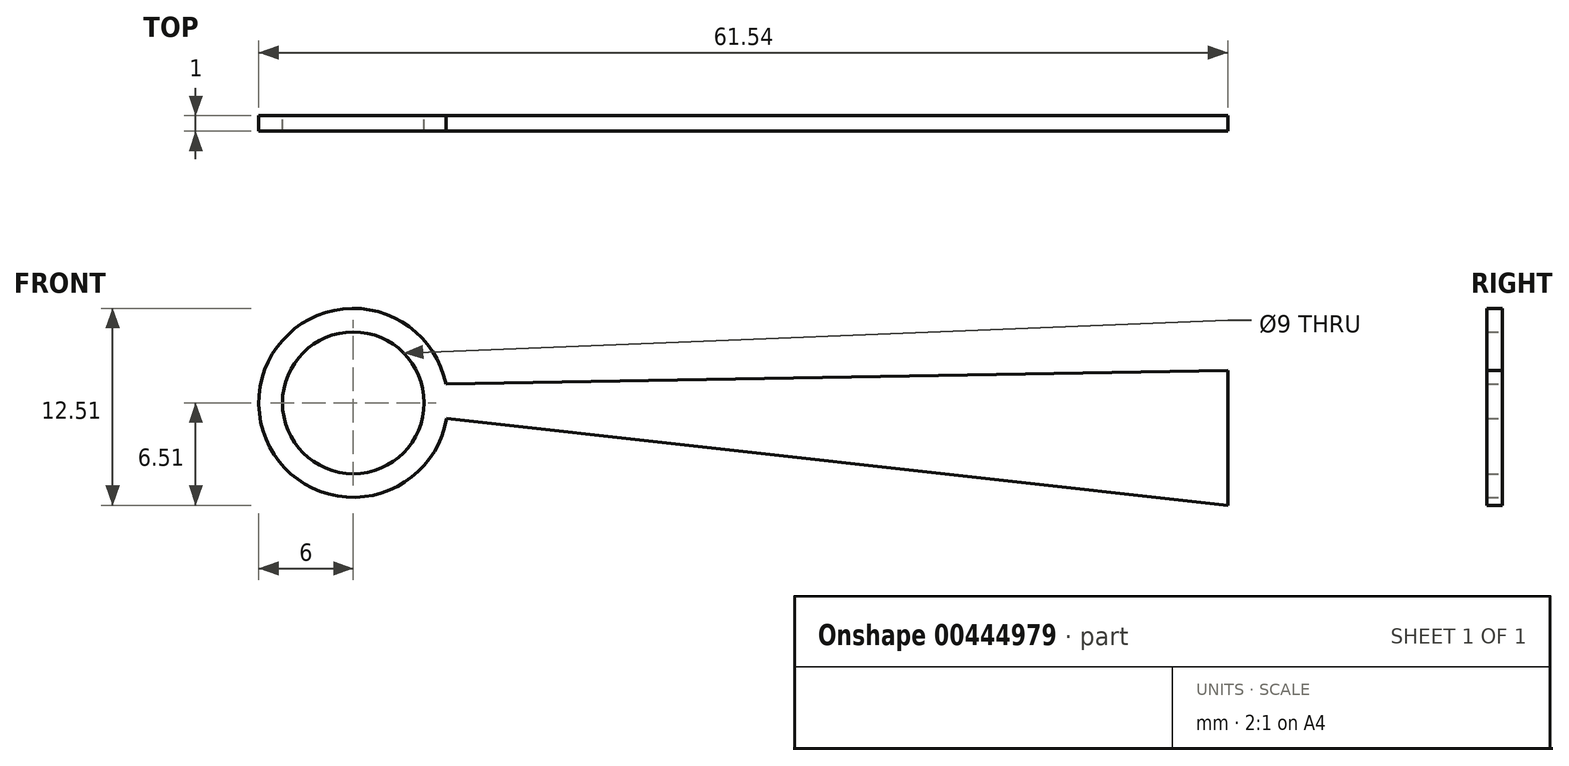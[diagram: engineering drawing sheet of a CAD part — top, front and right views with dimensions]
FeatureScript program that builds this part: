
annotation { "Feature Type Name" : "Feature", "Feature Type Description" : "" }
export const myFeature = defineFeature(function(context is Context, id is Id, definition is map)
    precondition{}
    {
        {
            var Q0;
            Q0=qCreatedBy(makeId("Front.planeOp"),FACE);
            var sketch = newSketch(context, id + "F0", { "sketchPlane" : qUnion([Q0])});
            skLineSegment(sketch, "E0", {"start": v(5.88, 1.19) * mm, "end": v(55.54, 2.05) * mm});
            skLineSegment(sketch, "E1", {"start": v(55.54, 2.05) * mm, "end": v(55.54, -6.51) * mm});
            skLineSegment(sketch, "E2", {"start": v(55.54, -6.51) * mm, "end": v(5.92, -0.98) * mm});
            skArc(sketch, "E3", {"start": v(5.88, 1.19) * mm, "mid": v(-6, -0.1) * mm, "end": v(5.92, -0.98) * mm});
            skPoint(sketch, "E4.center.orphan", {"position": v(-3.1, 0) * mm});
            skCircle(sketch, "E5", {"center": v(0, 0) * mm, "radius": 4.5 * mm});
            skSolve(sketch);
        }
        {
            var Q0;
            Q0 = qSketchRegion(id + "F0", true);
            extrude(context, id + "F1", {"entities" : qUnion([Q0]), "depth" : 1 * mm});
        }
    });
